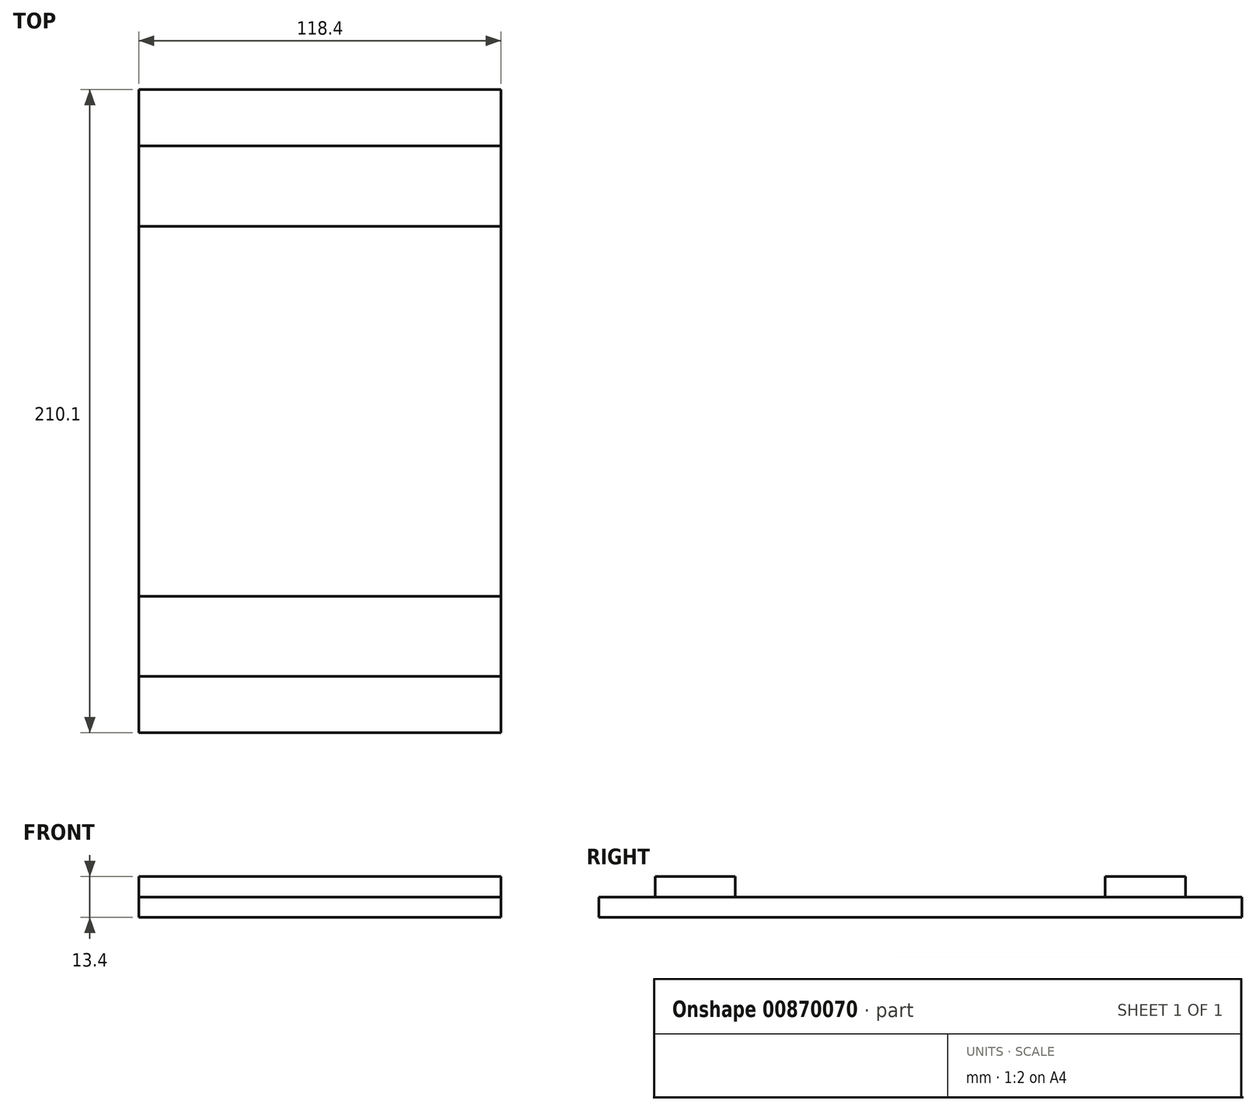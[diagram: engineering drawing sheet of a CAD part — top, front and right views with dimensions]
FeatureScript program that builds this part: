
annotation { "Feature Type Name" : "Feature", "Feature Type Description" : "" }
export const myFeature = defineFeature(function(context is Context, id is Id, definition is map)
    precondition{}
    {
        {
            assignVariable(context, id + "F0", {"name" : "width", "anyValue" : 6.7});
        }
        {
            var Q0;
            Q0=qCreatedBy(makeId("Top.planeOp"),FACE);
            var sketch = newSketch(context, id + "F1", { "sketchPlane" : qUnion([Q0])});
            skLineSegment(sketch, "E0.bottom", {"start": v(59.2, 105.05) * mm, "end": v(-59.2, 105.05) * mm});
            skLineSegment(sketch, "E0.top", {"start": v(59.2, -105.05) * mm, "end": v(-59.2, -105.05) * mm});
            skLineSegment(sketch, "E0.left", {"start": v(59.2, 105.05) * mm, "end": v(59.2, -105.05) * mm});
            skLineSegment(sketch, "E0.right", {"start": v(-59.2, 105.05) * mm, "end": v(-59.2, -105.05) * mm});
            skPoint(sketch, "E0.middle", {"position": v(0, 0) * mm});
            skSolve(sketch);
        }
        {
            var Q0;
            Q0=qSketchRegion(id+"F1",true);
            extrude(context, id + "F2", {"entities" : qUnion([Q0]), "depth" : (getVariable(context, 'width')) * mm, "offsetDistance" : 25 * mm});
        }
        {
            var Q0;
            Q0=makeQuery(id+"F2.opExtrude","CAP_FACE",FACE,{"disambiguationData":[OSD([sQuery(id+"F1.wireOp",EDGE,"E0.bottom"),sQuery(id+"F1.wireOp",EDGE,"E0.top"),sQuery(id+"F1.wireOp",EDGE,"E0.left"),sQuery(id+"F1.wireOp",EDGE,"E0.right")])],"isStart":false});
            var sketch = newSketch(context, id + "F3", { "sketchPlane" : qUnion([Q0])});
            skLineSegment(sketch, "E1.bottom", {"start": v(-59.2, -60.45) * mm, "end": v(59.2, -60.45) * mm});
            skLineSegment(sketch, "E1.top", {"start": v(-59.2, -86.7) * mm, "end": v(59.2, -86.7) * mm});
            skLineSegment(sketch, "E1.left", {"start": v(-59.2, -60.45) * mm, "end": v(-59.2, -86.7) * mm});
            skLineSegment(sketch, "E1.right", {"start": v(59.2, -60.45) * mm, "end": v(59.2, -86.7) * mm});
            skPoint(sketch, "E1.middle", {"position": v(0, -73.58) * mm});
            skPoint(sketch, "E1.middle.positionSnap0", {"position": v(0, -105.05) * mm});
            skPoint(sketch, "E1.centerSnap0", {"position": v(0, -105.05) * mm});
            skLineSegment(sketch, "E2.MirrorCS", {"start": v(-59.2, 60.45) * mm, "end": v(-59.2, 86.7) * mm});
            skLineSegment(sketch, "E3.MirrorCS", {"start": v(59.2, 60.45) * mm, "end": v(59.2, 86.7) * mm});
            skLineSegment(sketch, "E4.MirrorCS", {"start": v(-59.2, 86.7) * mm, "end": v(59.2, 86.7) * mm});
            skLineSegment(sketch, "E5.MirrorCS", {"start": v(-59.2, 60.45) * mm, "end": v(59.2, 60.45) * mm});
            skPoint(sketch, "E6.MirrorP", {"position": v(0, 73.58) * mm});
            skSolve(sketch);
        }
        {
            var Q0;
            Q0=makeQuery(id+"F3.imprint","IMPRINT",FACE,{"disambiguationData":[TD([[makeQuery(id+"F3.imprint","IMPRINT",EDGE,{"derivedFrom":sQuery(id+"F3.wireOp",EDGE,"E1.bottom")}),-1.0]])]});
            var Q1;
            Q1=makeQuery(id+"F3.imprint","IMPRINT",FACE,{"disambiguationData":[TD([[makeQuery(id+"F3.imprint","IMPRINT",EDGE,{"derivedFrom":sQuery(id+"F3.wireOp",EDGE,"E2.MirrorCS")}),1.0]])]});
            extrude(context, id + "F4", {"entities" : qUnion([Q0, Q1]), "depth" : (getVariable(context, 'width')) * mm, "offsetDistance" : 25 * mm});
        }
    });
